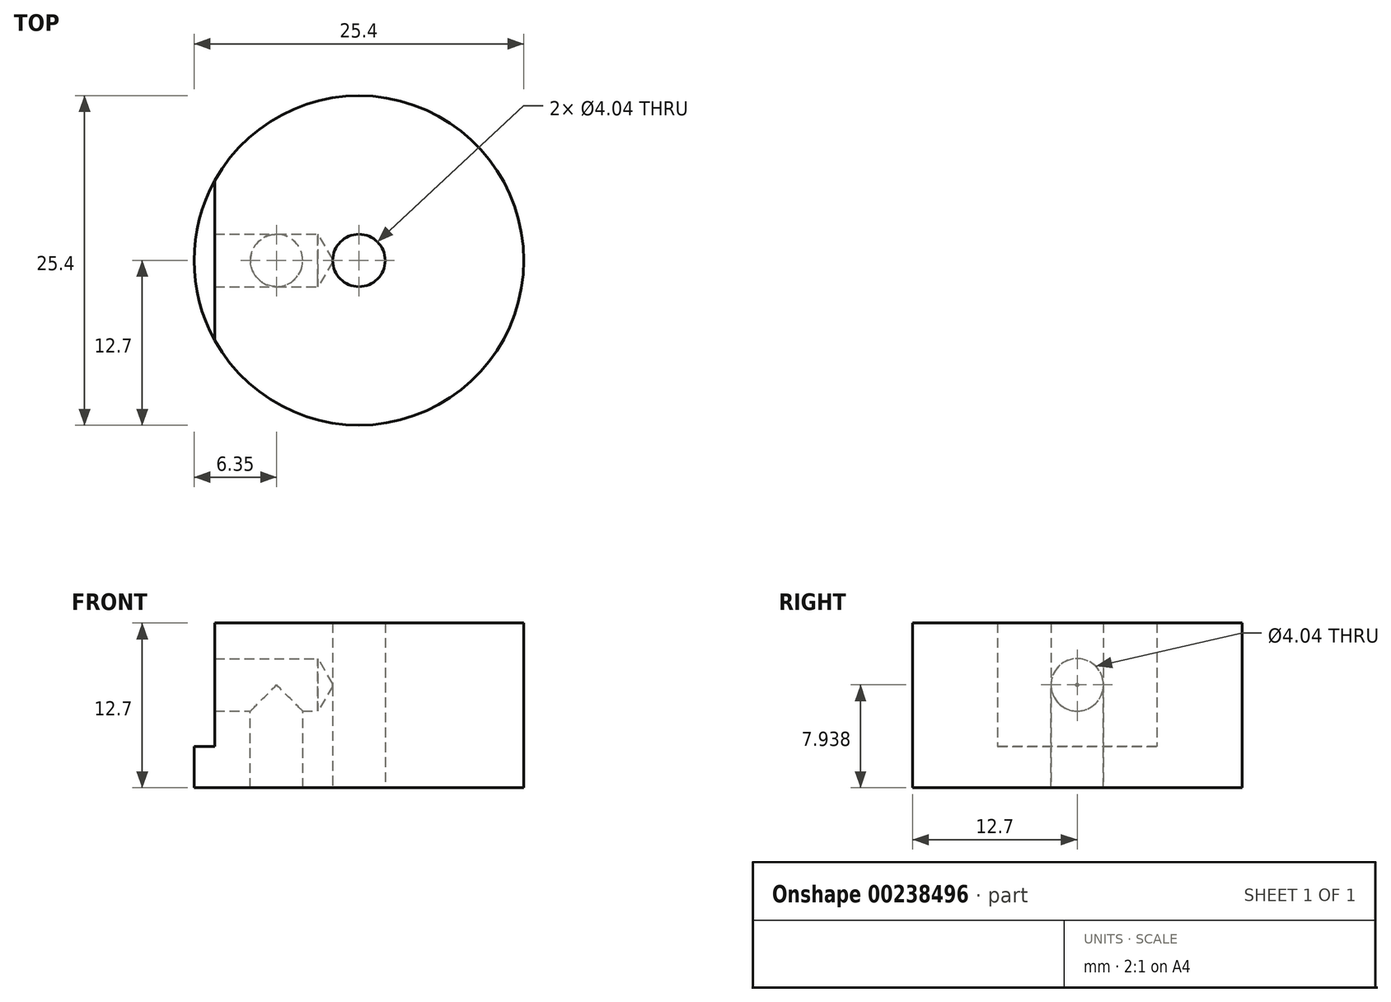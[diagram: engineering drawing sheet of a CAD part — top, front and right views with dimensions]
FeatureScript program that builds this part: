
annotation { "Feature Type Name" : "Feature", "Feature Type Description" : "" }
export const myFeature = defineFeature(function(context is Context, id is Id, definition is map)
    precondition{}
    {
        {
            var Q0;
            Q0=qCreatedBy(makeId("Top.planeOp"),FACE);
            var sketch = newSketch(context, id + "F0", { "sketchPlane" : qUnion([Q0])});
            skCircle(sketch, "E0", {"center": v(0, 0) * mm, "radius": 12.7 * mm});
            skCircle(sketch, "E1", {"center": v(0, 0) * mm, "radius": 2.02 * mm});
            skSolve(sketch);
        }
        {
            var Q0;
            Q0 = qSketchRegion(id + "F0", true);
            extrude(context, id + "F1", {"entities" : qUnion([Q0]), "depth" : 12.7 * mm});
        }
        {
            var Q0;
            Q0=qCreatedBy(makeId("Front.planeOp"),FACE);
            var sketch = newSketch(context, id + "F2", { "sketchPlane" : qUnion([Q0])});
            skLineSegment(sketch, "E2.bottom", {"start": v(-14.29, 3.18) * mm, "end": v(-11.11, 3.18) * mm});
            skLineSegment(sketch, "E2.top", {"start": v(-14.29, 15.88) * mm, "end": v(-11.11, 15.88) * mm});
            skLineSegment(sketch, "E2.left", {"start": v(-14.29, 3.18) * mm, "end": v(-14.29, 15.88) * mm});
            skLineSegment(sketch, "E2.right", {"start": v(-11.11, 3.18) * mm, "end": v(-11.11, 15.88) * mm});
            skPoint(sketch, "E2.middle", {"position": v(-12.7, 9.52) * mm});
            skSolve(sketch);
        }
        {
            var Q0;
            Q0 = qSketchRegion(id + "F2", true);
            extrude(context, id + "F3", {"entities" : qUnion([Q0]), "operationType" : NewBodyOperationType.REMOVE, "depth" : 25.4 * mm, "symmetric" : true});
        }
        {
            var Q0;
            Q0=makeQuery(id+"F3.boolean.opBoolean","COPY",FACE,{"derivedFrom":makeQuery(id+"F3.opExtrude","SWEPT_FACE",FACE,{"disambiguationData":[OSD([sQuery(id+"F2.wireOp",EDGE,"E2.right")])]})});
            var sketch = newSketch(context, id + "F4", { "sketchPlane" : qUnion([Q0])});
            skPoint(sketch, "E3", {"position": v(0, 7.94) * mm});
            skSolve(sketch);
        }
        {
            var Q0;
            Q0=sQuery(id+"F4.wireOp",VERTEX,"E3");
            var Q1;
            Q1=makeQuery(id+"F1.opExtrude","SWEPT_BODY",BODY,{"disambiguationData":[OSD([sQuery(id+"F0.wireOp",EDGE,"E0"),sQuery(id+"F0.wireOp",EDGE,"E1")])]});
            hole(context, id + "F5", {"style" : HoleStyle.SIMPLE, "endStyle" : HoleEndStyle.BLIND, "standardTappedOrClearance" : lookupTablePath({ "standard" : "ANSI", "engagement" : "75%", "pitch" : "32 tpi", "size" : "#10", "type" : "Tapped" }), "standardBlindInLast" : lookupTablePath({ "standard" : "ANSI", "engagement" : "75%", "pitch" : "32 tpi", "size" : "#10", "type" : "Tapped" }), "holeDiameter" : 4.04 * mm, "showTappedDepth" : true, "holeDepth" : 7.95 * mm, "tappedDepth" : 5.57 * mm, "tapClearance" : 3, "locations" : qUnion([Q0]), "scope" : qUnion([Q1]), "majorDiameter" : 4.83 * mm, "startStyle" : HoleStartStyle.PART});
        }
        {
            var Q0;
            Q0=makeQuery(id+"F1.opExtrude","CAP_FACE",FACE,{"disambiguationData":[OSD([sQuery(id+"F0.wireOp",EDGE,"E0"),sQuery(id+"F0.wireOp",EDGE,"E1")])],"isStart":true});
            var sketch = newSketch(context, id + "F6", { "sketchPlane" : qUnion([Q0])});
            skPoint(sketch, "E4", {"position": v(-6.35, 0) * mm});
            skSolve(sketch);
        }
        {
            var Q0;
            Q0=sQuery(id+"F6.wireOp",VERTEX,"E4");
            var Q1;
            Q1=makeQuery(id+"F1.opExtrude","SWEPT_BODY",BODY,{"disambiguationData":[OSD([sQuery(id+"F0.wireOp",EDGE,"E0"),sQuery(id+"F0.wireOp",EDGE,"E1")])]});
            hole(context, id + "F7", {"style" : HoleStyle.SIMPLE, "endStyle" : HoleEndStyle.BLIND, "standardTappedOrClearance" : lookupTablePath({ "standard" : "ANSI", "engagement" : "75%", "pitch" : "32 tpi", "size" : "#10", "type" : "Tapped" }), "standardBlindInLast" : lookupTablePath({ "standard" : "ANSI", "engagement" : "75%", "pitch" : "32 tpi", "size" : "#10", "type" : "Tapped" }), "holeDiameter" : 4.04 * mm, "showTappedDepth" : true, "holeDepth" : 7.95 * mm, "tappedDepth" : 5.57 * mm, "tapClearance" : 3, "locations" : qUnion([Q0]), "scope" : qUnion([Q1]), "majorDiameter" : 4.83 * mm, "startStyle" : HoleStartStyle.PART});
        }
    });
